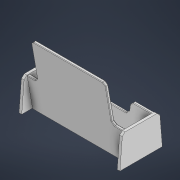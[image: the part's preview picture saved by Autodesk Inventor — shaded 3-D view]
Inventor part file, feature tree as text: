
AUTODESK INVENTOR PART (.ipt)
format: ipt  version: 2021 (Build 250183000, 183)  size: 2,143,744 bytes
history: native  units: mm
features: extrude x5, sketch x5, other x3, chamfer x2, mirror x1
ambient origin geometry x8: Origin, YZ Plane, XZ Plane, XY Plane, X Axis, Y Axis, Z Axis, Center Point
bodies: Solid1 (feature_tree)
feature tree (16):
  other  "Blocks"
  extrude  "Extrusion1"  Depth=35.0mm
  extrude  "Extrusion2"  TaperAngle=0.0deg  [1 undecoded]
  extrude  "Extrusion5"  Depth=2.5mm
  extrude  "Extrusion6"  Depth=2.5mm
  chamfer  "Chamfer1"  Distance=17.453293mm
  chamfer  "Chamfer2"  Distance=17.453293mm
  mirror  "Mirror2"
  extrude  "Extrusion7"  Depth=45.0mm TaperAngle=0.0deg
  sketch  "Sketch2"  dims[d4=30.0mm d5=35.0mm]
  sketch  "Sketch5"  dims[d6=40.0mm d14=0.0mm]
  sketch  "Sketch8"  dims[d15=2.5mm d16=2.5mm]
  sketch  "Sketch9"  dims[d17=2.5mm d18=2.5mm]
  sketch  "Sketch10"  dims[d19=2.5mm d22=17.453293mm d23=17.453293mm d24=45.0mm d25=0.0mm d33=10.0mm d34=25.0mm d35=2.5mm d36=0.0mm d38=10.0mm d39=2.5mm d40=0.0mm d43=65.0mm d44=2.5mm d45=2.0mm d46=45.0deg d47=0.5mm d48=2.0mm d49=45.0deg d50=1.5mm d51=0.0mm]
  other  "lgcc"
  other  "lgcc:1"
note: 1 required parameter value undecoded (feature->parameter linkage not recoverable at this tier; creation-order binding heuristic only, values carry confidence <= 0.55)
